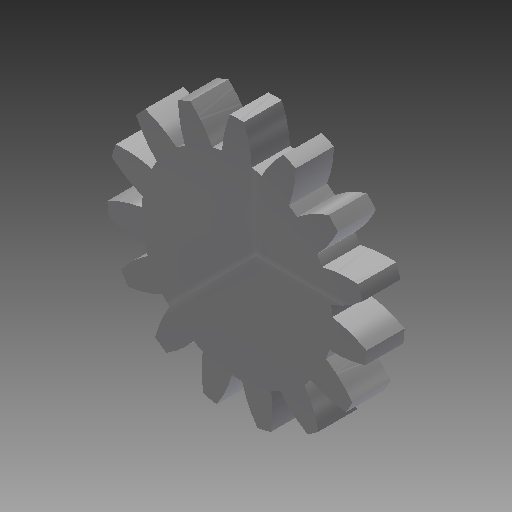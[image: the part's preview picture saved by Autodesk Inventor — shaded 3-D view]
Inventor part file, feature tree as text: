
AUTODESK INVENTOR PART (.ipt)
format: ipt  version: 2017 (Build 210142000, 142)  size: 197,120 bytes
history: native  units: mm (DEFAULTED — no unit token found)
features: plane x3, other x3, sketch x2, extrude x1
ambient origin geometry x8: Origin, YZ Plane, XZ Plane, XY Plane, X Axis, Y Axis, Z Axis, Center Point
bodies: Solid1 (feature_tree)
feature tree (9):
  extrude  "Extrusion1"  Depth=6.35mm TaperAngle=0.0deg
  plane  "Work Plane1"
  plane  "Work Plane2"
  plane  "Work Plane3"
  other  "Spur Gear"
  sketch  "Sketch1"  dims[d0=43.18mm d1=6.35mm d2=0.0mm]
  sketch  "Sketch2"  dims[d3=38.1mm d4=76.2mm d5=0.0mm d6=0.0mm d7=2.094395mm d9=0.0mm d14=0.0mm d15=173.99mm d16=0.0mm d17=0.0mm d18=0.0mm d19=173.99mm]
  other  "Srf1"
  other  "Pitch Diameter"
